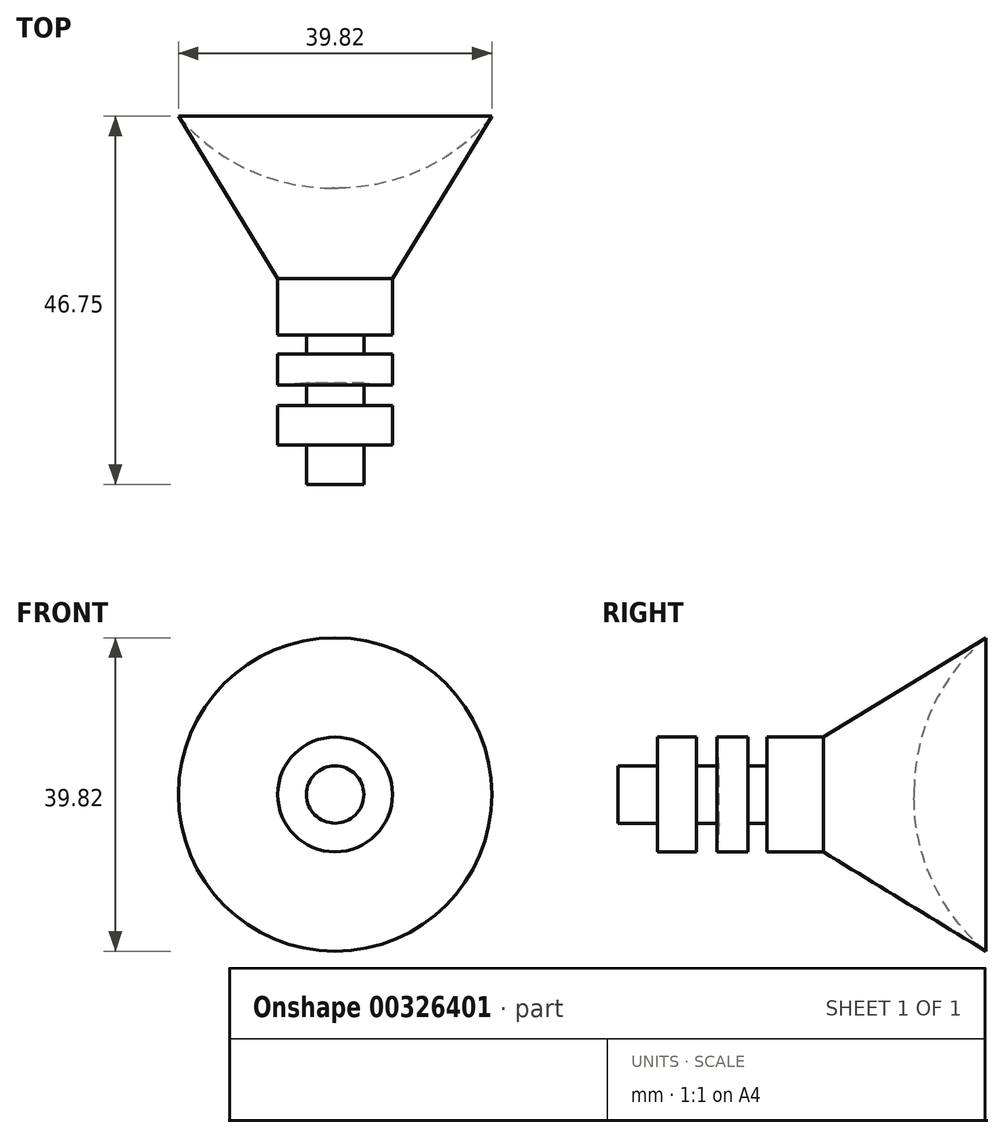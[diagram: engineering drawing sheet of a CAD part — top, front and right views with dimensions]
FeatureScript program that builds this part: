
annotation { "Feature Type Name" : "Feature", "Feature Type Description" : "" }
export const myFeature = defineFeature(function(context is Context, id is Id, definition is map)
    precondition{}
    {
        {
            var Q0;
            Q0=qCreatedBy(makeId("Top.planeOp"),FACE);
            var sketch = newSketch(context, id + "F0", { "sketchPlane" : qUnion([Q0])});
            skArc(sketch, "E0", {"start": v(0, 35.44) * mm, "mid": v(-23.38, 20.93) * mm, "end": v(-19.91, -6.36) * mm});
            skLineSegment(sketch, "E1", {"start": v(0, -40.05) * mm, "end": v(0, 35.44) * mm});
            skPoint(sketch, "E2.orphan", {"position": v(0, -15.47) * mm});
            skLineSegment(sketch, "E3.bottom", {"start": v(0, -27) * mm, "end": v(-7.3, -27) * mm});
            skLineSegment(sketch, "E3.top", {"start": v(0, -53.1) * mm, "end": v(-3.65, -53.1) * mm});
            skLineSegment(sketch, "E3.right", {"start": v(-7.3, -27) * mm, "end": v(-7.3, -34.18) * mm});
            skPoint(sketch, "E3.middle", {"position": v(0, -40.05) * mm});
            skLineSegment(sketch, "E4", {"start": v(-7.3, -34.18) * mm, "end": v(-3.65, -34.18) * mm});
            skLineSegment(sketch, "E5", {"start": v(-3.65, -36.57) * mm, "end": v(-7.3, -36.57) * mm});
            skLineSegment(sketch, "E6.trimOffspring", {"start": v(-7.3, -36.57) * mm, "end": v(-7.3, -40.49) * mm});
            skLineSegment(sketch, "E7", {"start": v(0, -40.05) * mm, "end": v(0, -53.1) * mm});
            skPoint(sketch, "E3.left.start.orphan", {"position": v(7.3, -27) * mm});
            skPoint(sketch, "E8.orphan", {"position": v(7.3, -53.1) * mm});
            skLineSegment(sketch, "E9", {"start": v(-7.3, -43.1) * mm, "end": v(-3.65, -43.1) * mm});
            skLineSegment(sketch, "E10", {"start": v(-7.3, -40.49) * mm, "end": v(-3.65, -40.27) * mm});
            skLineSegment(sketch, "E11.trimOffspring", {"start": v(-7.3, -43.1) * mm, "end": v(-7.3, -48.1) * mm});
            skLineSegment(sketch, "E12", {"start": v(-19.91, -6.36) * mm, "end": v(-7.3, -27) * mm});
            skLineSegment(sketch, "E13", {"start": v(-3.65, -43.1) * mm, "end": v(-3.65, -40.05) * mm});
            skPoint(sketch, "E14.orphan", {"position": v(0, -43.1) * mm});
            skLineSegment(sketch, "E15", {"start": v(-3.65, -36.57) * mm, "end": v(-3.65, -34.18) * mm});
            skPoint(sketch, "E16.orphan", {"position": v(0, -36.57) * mm});
            skPoint(sketch, "E17.orphan", {"position": v(0, -34.18) * mm});
            skPoint(sketch, "E18.end.orphan", {"position": v(-3.65, -48.1) * mm});
            skPoint(sketch, "E18.start.orphan", {"position": v(-7.3, -48.1) * mm});
            skPoint(sketch, "E19.endSnap0", {"position": v(-3.65, -53.1) * mm});
            skLineSegment(sketch, "E20", {"start": v(-3.65, -52.45) * mm, "end": v(-3.65, -48.1) * mm});
            skLineSegment(sketch, "E21", {"start": v(-3.65, -48.1) * mm, "end": v(-7.3, -48.1) * mm});
            skLineSegment(sketch, "E22", {"start": v(-3.65, -53.1) * mm, "end": v(-3.65, -52.45) * mm});
            skPoint(sketch, "E23.trimOffspring.end.orphan", {"position": v(-7.3, -53.1) * mm});
            skSolve(sketch);
        }
        {
            var Q0;
            Q0 = qSketchRegion(id + "F0", true);
            var Q1;
            Q1=sQuery(id+"F0.wireOp",EDGE,"E1");
            revolve(context, id + "F1", {"entities" : qUnion([Q0]), "axis" : qUnion([Q1]), "revolveType" : RevolveType.FULL});
        }
    });
